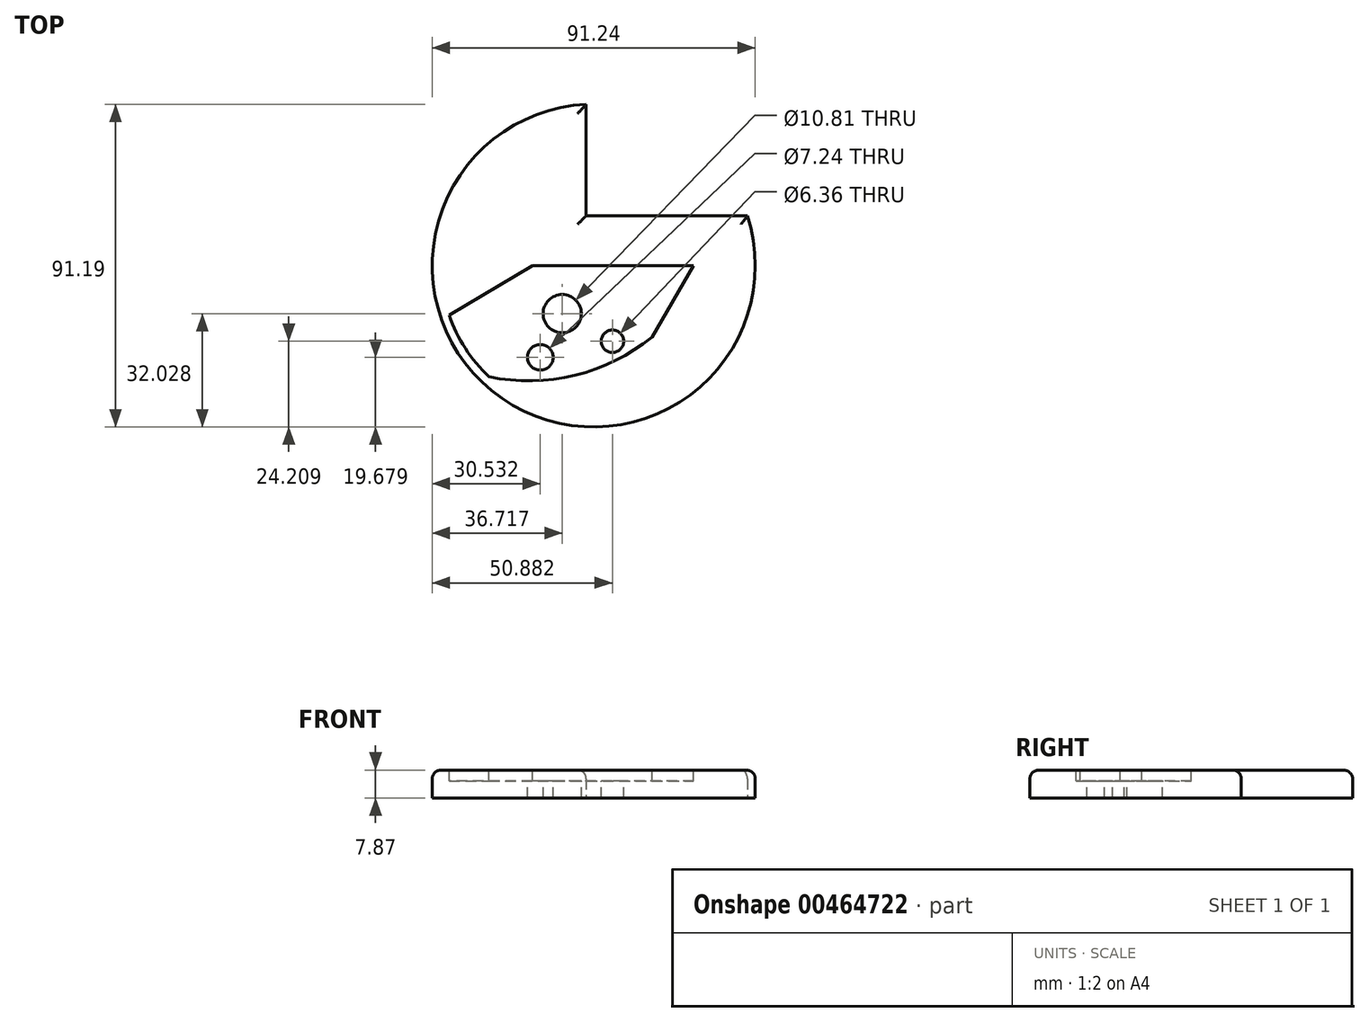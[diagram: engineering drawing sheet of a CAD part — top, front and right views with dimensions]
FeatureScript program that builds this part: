
annotation { "Feature Type Name" : "Feature", "Feature Type Description" : "" }
export const myFeature = defineFeature(function(context is Context, id is Id, definition is map)
    precondition{}
    {
        {
            var Q0;
            Q0=qCreatedBy(makeId("Top.planeOp"),FACE);
            var sketch = newSketch(context, id + "F0", { "sketchPlane" : qUnion([Q0])});
            skArc(sketch, "E0", {"start": v(-2.13, 45.57) * mm, "mid": v(-25.95, -37.52) * mm, "end": v(43.4, 14.09) * mm});
            skLineSegment(sketch, "E1.top", {"start": v(-2.13, 14.09) * mm, "end": v(43.4, 14.09) * mm});
            skLineSegment(sketch, "E1.left", {"start": v(-2.13, 45.57) * mm, "end": v(-2.13, 14.09) * mm});
            skSolve(sketch);
        }
        {
            var Q0;
            Q0=makeQuery(id+"F0.imprint","IMPRINT",FACE,{"disambiguationData":[TD([[makeQuery(id+"F0.imprint","IMPRINT",EDGE,{"derivedFrom":sQuery(id+"F0.wireOp",EDGE,"E0")}),1.0]])]});
            extrude(context, id + "F1", {"entities" : qUnion([Q0]), "depth" : 7.87 * mm, "offsetDistance" : 25.4 * mm});
        }
        {
            var Q0;
            Q0=makeQuery(id+"F1.opExtrude","CAP_FACE",FACE,{"disambiguationData":[OSD([sQuery(id+"F0.wireOp",EDGE,"E0"),sQuery(id+"F0.wireOp",EDGE,"E1.top"),sQuery(id+"F0.wireOp",EDGE,"E1.left")])],"isStart":false});
            fillet(context, id + "F2", {"entities" : qUnion([Q0]), "radius" : 2.45 * mm, "tangentPropagation" : true, "allowEdgeOverflow" : false});
        }
        {
            var Q0;
            Q0=makeQuery(id+"F1.opExtrude","CAP_FACE",FACE,{"disambiguationData":[OSD([sQuery(id+"F0.wireOp",EDGE,"E0"),sQuery(id+"F0.wireOp",EDGE,"E1.top"),sQuery(id+"F0.wireOp",EDGE,"E1.left")])],"isStart":false});
            var sketch = newSketch(context, id + "F3", { "sketchPlane" : qUnion([Q0])});
            skArc(sketch, "E2", {"start": v(-52.26, -20.86) * mm, "mid": v(-17.79, -32.58) * mm, "end": v(16.44, -20.17) * mm});
            skLineSegment(sketch, "E3", {"start": v(16.44, -20.17) * mm, "end": v(28.2, 0) * mm});
            skLineSegment(sketch, "E4", {"start": v(28.2, 0) * mm, "end": v(-17.35, 0) * mm});
            skLineSegment(sketch, "E5", {"start": v(-17.35, 0) * mm, "end": v(-52.26, -20.86) * mm});
            skSolve(sketch);
        }
        {
            var Q0;
            {var subQ5=sQuery(id+"F3.wireOp",EDGE,"E3");Q0=makeQuery(id+"F3.imprint","IMPRINT",FACE,{"disambiguationData":[TD([[makeQuery(id+"F3.imprint","IMPRINT",EDGE,{"derivedFrom":subQ5}),1.0]])]});}
            extrude(context, id + "F4", {"entities" : qUnion([Q0]), "operationType" : NewBodyOperationType.REMOVE, "oppositeDirection" : true, "depth" : 3.05 * mm, "offsetDistance" : 25.4 * mm});
        }
        {
            var Q0;
            Q0=makeQuery(id+"F4.boolean.opBoolean","COPY",FACE,{"derivedFrom":makeQuery(id+"F4.opExtrude","CAP_FACE",FACE,{"disambiguationData":[OSD([sQuery(id+"F0.wireOp",EDGE,"E0"),sQuery(id+"F0.wireOp",EDGE,"E1.top"),sQuery(id+"F0.wireOp",EDGE,"E1.left"),sQuery(id+"F3.wireOp",EDGE,"E2"),sQuery(id+"F3.wireOp",EDGE,"E3"),sQuery(id+"F3.wireOp",EDGE,"E4"),sQuery(id+"F3.wireOp",EDGE,"E5")])],"isStart":false})});
            var sketch = newSketch(context, id + "F5", { "sketchPlane" : qUnion([Q0])});
            skCircle(sketch, "E6", {"center": v(5.26, -21.41) * mm, "radius": 3.18 * mm});
            skCircle(sketch, "E7", {"center": v(-15.09, -25.94) * mm, "radius": 3.62 * mm});
            skCircle(sketch, "E8", {"center": v(-8.9, -13.6) * mm, "radius": 5.4 * mm});
            skSolve(sketch);
        }
        {
            var Q0;
            Q0=makeQuery(id+"F5.imprint","IMPRINT",FACE,{"disambiguationData":[TD([[makeQuery(id+"F5.imprint","IMPRINT",EDGE,{"derivedFrom":sQuery(id+"F5.wireOp",EDGE,"E8")}),1.0]])]});
            var Q1;
            Q1=makeQuery(id+"F5.imprint","IMPRINT",FACE,{"disambiguationData":[TD([[makeQuery(id+"F5.imprint","IMPRINT",EDGE,{"derivedFrom":sQuery(id+"F5.wireOp",EDGE,"E7")}),1.0]])]});
            var Q2;
            Q2=makeQuery(id+"F5.imprint","IMPRINT",FACE,{"disambiguationData":[TD([[makeQuery(id+"F5.imprint","IMPRINT",EDGE,{"derivedFrom":sQuery(id+"F5.wireOp",EDGE,"E6")}),1.0]])]});
            extrude(context, id + "F6", {"entities" : qUnion([Q0, Q1, Q2]), "operationType" : NewBodyOperationType.REMOVE, "oppositeDirection" : true, "depth" : 25.4 * mm, "offsetDistance" : 25.4 * mm});
        }
    });
